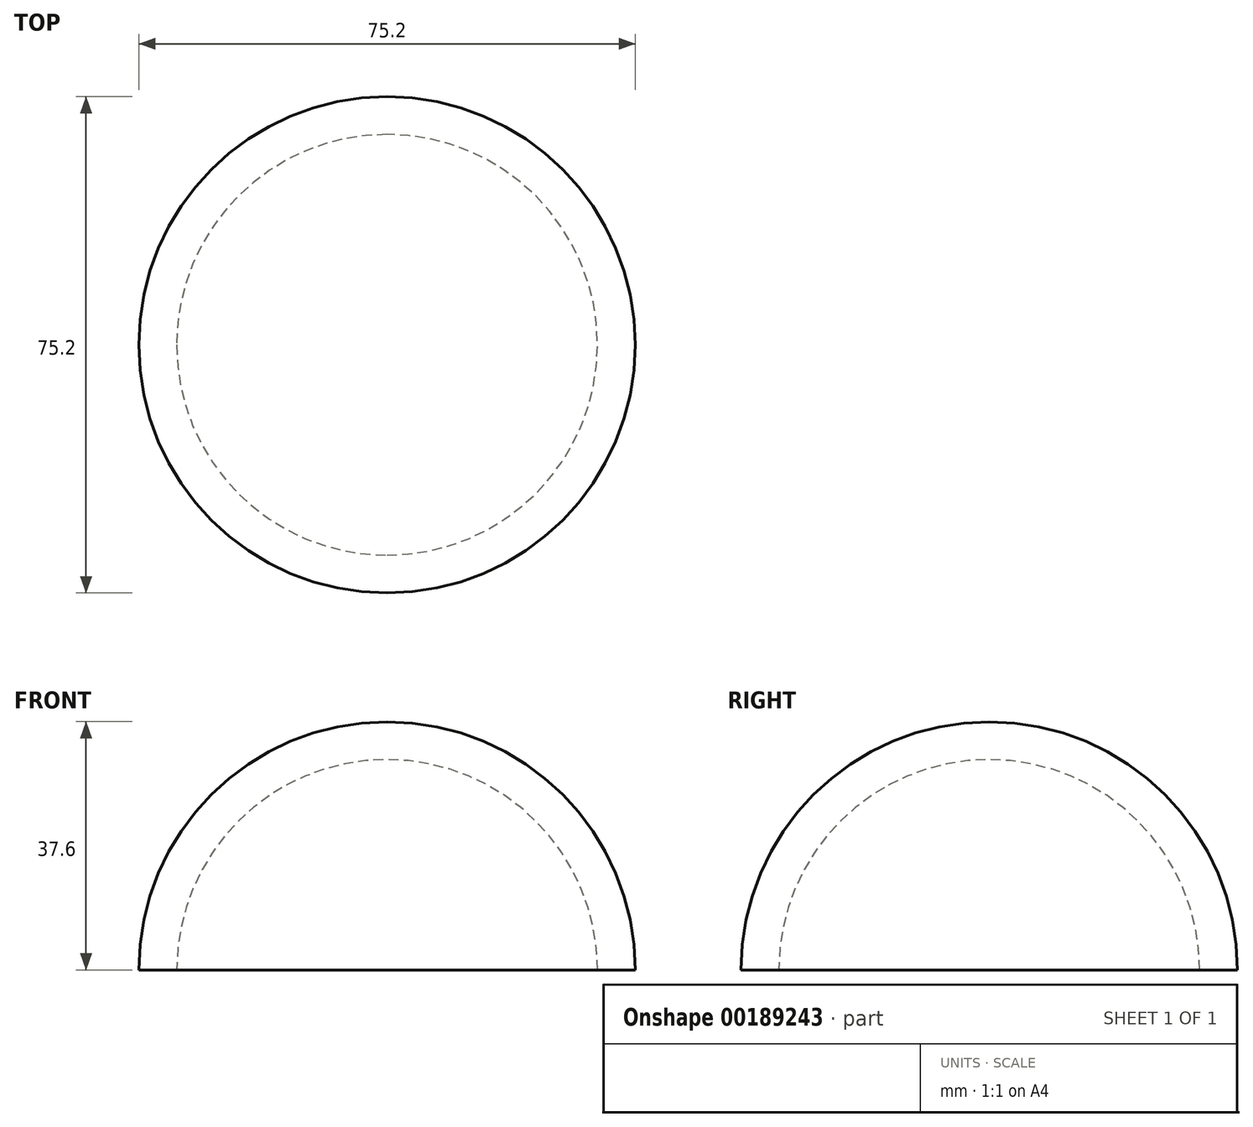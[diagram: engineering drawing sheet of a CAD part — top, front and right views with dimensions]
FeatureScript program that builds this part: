
annotation { "Feature Type Name" : "Feature", "Feature Type Description" : "" }
export const myFeature = defineFeature(function(context is Context, id is Id, definition is map)
    precondition{}
    {
        {
            var Q0;
            Q0=qCreatedBy(makeId("Top.planeOp"),FACE);
            var sketch = newSketch(context, id + "F0", { "sketchPlane" : qUnion([Q0])});
            skArc(sketch, "E0", {"start": v(0, 37.6) * mm, "mid": v(-37.6, 0) * mm, "end": v(0, -37.6) * mm});
            skArc(sketch, "E1", {"start": v(0, 31.86) * mm, "mid": v(-31.86, 0) * mm, "end": v(0, -31.86) * mm});
            skLineSegment(sketch, "E2", {"start": v(0, -37.6) * mm, "end": v(0, 37.6) * mm});
            skSolve(sketch);
        }
        {
            var Q0;
            {var subQ0=sQuery(id+"F0.wireOp",EDGE,"E0");Q0=makeQuery(id+"F0.imprint","IMPRINT",FACE,{"disambiguationData":[TD([[makeQuery(id+"F0.imprint","IMPRINT",EDGE,{"derivedFrom":subQ0}),1.0]])]});}
            var Q1;
            Q1=sQuery(id+"F0.wireOp",EDGE,"E2");
            revolve(context, id + "F1", {"entities" : qUnion([Q0]), "axis" : qUnion([Q1]), "revolveType" : RevolveType.ONE_DIRECTION, "angle" : 180 * degree});
        }
    });
